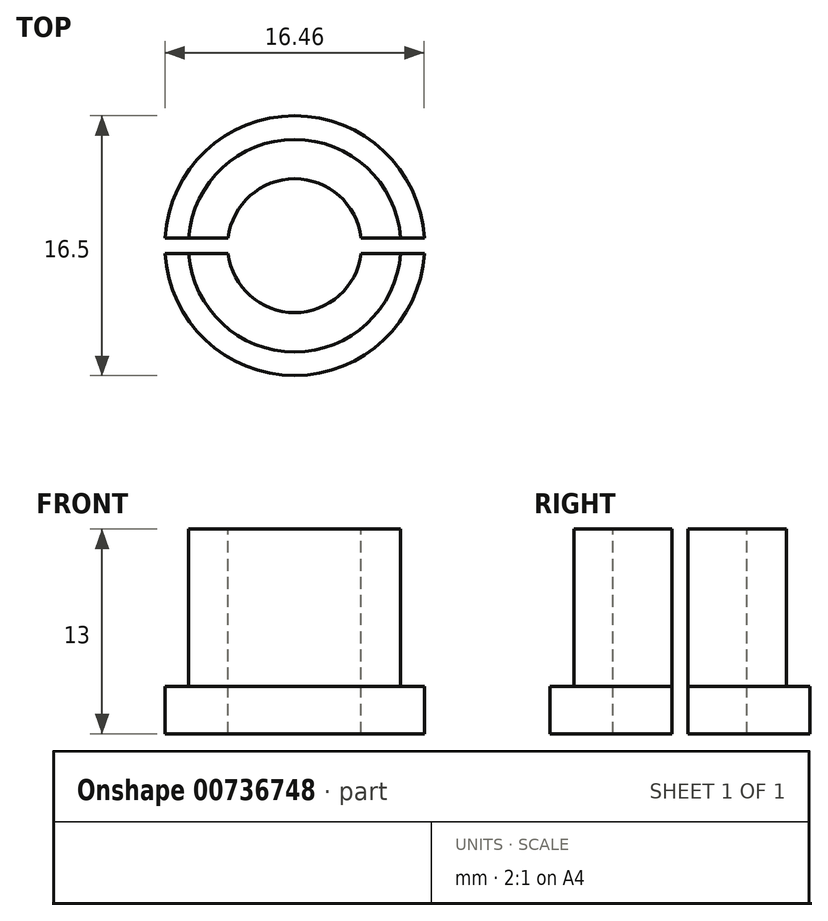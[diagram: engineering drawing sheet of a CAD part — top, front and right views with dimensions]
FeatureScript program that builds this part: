
annotation { "Feature Type Name" : "Feature", "Feature Type Description" : "" }
export const myFeature = defineFeature(function(context is Context, id is Id, definition is map)
    precondition{}
    {
        {
            var Q0;
            Q0=qCreatedBy(makeId("Front.planeOp"),FACE);
            var sketch = newSketch(context, id + "F0", { "sketchPlane" : qUnion([Q0])});
            skLineSegment(sketch, "E0", {"start": v(-8.25, 0) * mm, "end": v(-8.25, 3) * mm});
            skLineSegment(sketch, "E1", {"start": v(-8.25, 3) * mm, "end": v(-6.75, 3) * mm});
            skLineSegment(sketch, "E2", {"start": v(-6.75, 3) * mm, "end": v(-6.75, 13) * mm});
            skLineSegment(sketch, "E3", {"start": v(-4.25, 0) * mm, "end": v(-8.25, 0) * mm});
            skLineSegment(sketch, "E4", {"start": v(-6.75, 13) * mm, "end": v(-4.25, 13) * mm});
            skLineSegment(sketch, "E5", {"start": v(-4.25, 13) * mm, "end": v(-4.25, 0) * mm});
            skLineSegment(sketch, "E6", {"start": v(0, 13) * mm, "end": v(0, 0) * mm, "construction": true});
            skLineSegment(sketch, "E7", {"start": v(-4.25, 13) * mm, "end": v(0, 13) * mm, "construction": true});
            skSolve(sketch);
        }
        {
            var Q0;
            Q0 = qSketchRegion(id + "F0", true);
            var Q1;
            Q1=sQuery(id+"F0.wireOp",EDGE,"E6");
            revolve(context, id + "F1", {"surfaceOperationType" : NewSurfaceOperationType.NEW, "entities" : qUnion([Q0]), "axis" : qUnion([Q1]), "revolveType" : RevolveType.FULL});
        }
        {
            var Q0;
            Q0=qCreatedBy(makeId("Right.planeOp"),FACE);
            var sketch = newSketch(context, id + "F2", { "sketchPlane" : qUnion([Q0])});
            skLineSegment(sketch, "E8.bottom", {"start": v(0.5, 13) * mm, "end": v(-0.5, 13) * mm});
            skLineSegment(sketch, "E8.top", {"start": v(0.5, 0) * mm, "end": v(-0.5, 0) * mm});
            skLineSegment(sketch, "E8.left", {"start": v(0.5, 13) * mm, "end": v(0.5, 0) * mm});
            skLineSegment(sketch, "E8.right", {"start": v(-0.5, 13) * mm, "end": v(-0.5, 0) * mm});
            skSolve(sketch);
        }
        {
            var Q0;
            Q0 = qSketchRegion(id + "F2", true);
            extrude(context, id + "F3", {"entities" : qUnion([Q0]), "operationType" : NewBodyOperationType.REMOVE, "oppositeDirection" : true, "depth" : 25.4 * mm, "offsetDistance" : 25.4 * mm});
        }
        {
            var Q0;
            Q0 = qSketchRegion(id + "F2", true);
            extrude(context, id + "F4", {"entities" : qUnion([Q0]), "operationType" : NewBodyOperationType.REMOVE, "depth" : 25.4 * mm, "offsetDistance" : 25.4 * mm});
        }
    });
